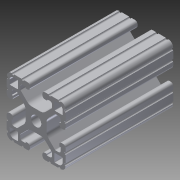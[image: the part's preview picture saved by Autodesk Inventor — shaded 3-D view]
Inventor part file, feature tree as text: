
AUTODESK INVENTOR PART (.ipt)
format: ipt  version: 2013 (Build 170138000, 138)  size: 308,736 bytes
history: native  units: in
note: dims shown in document units (in); Inventor stores cm internally (conversion verified against a paired STEP export)
features: extrude x1, sketch x1
ambient origin geometry x8: Origin, YZ Plane, XZ Plane, XY Plane, X Axis, Y Axis, Z Axis, Center Point
bodies: Solid1 (feature_tree)
feature tree (2):
  extrude  "Extrusion1"  [1 undecoded]
  sketch  "Sketch1"  dims[d0=2.75in d1=0.0in]
note: 1 required parameter value undecoded (feature->parameter linkage not recoverable at this tier; creation-order binding heuristic only, values carry confidence <= 0.55)
